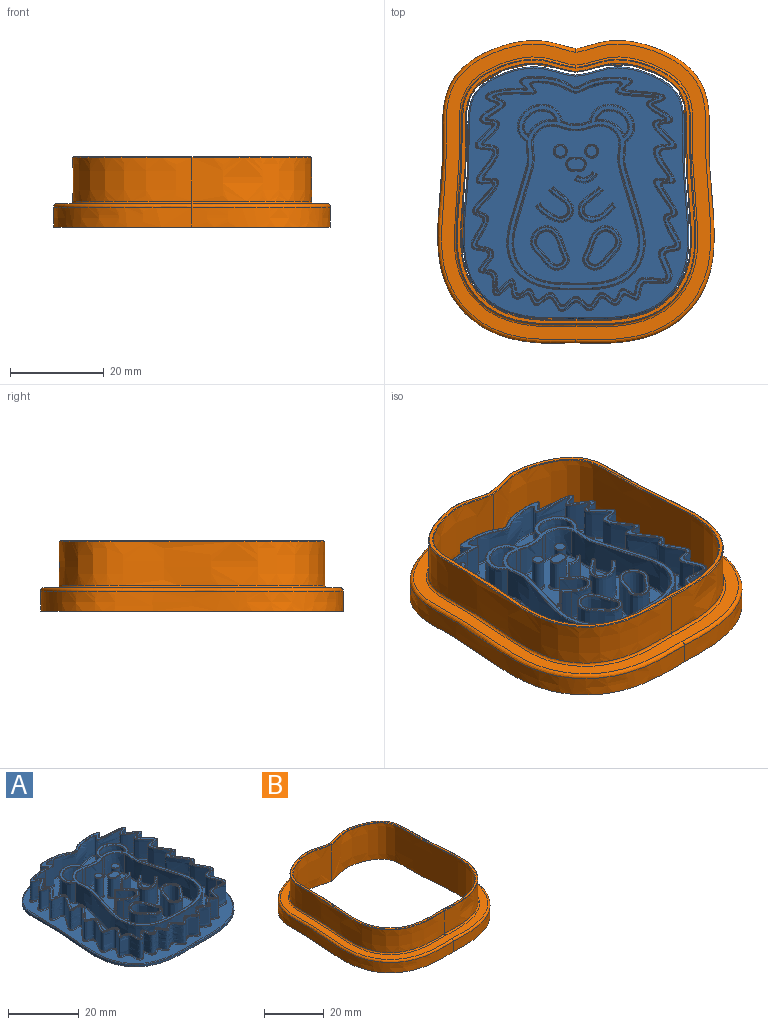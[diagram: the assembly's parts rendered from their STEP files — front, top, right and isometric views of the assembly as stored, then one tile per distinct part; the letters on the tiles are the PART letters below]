
ASSEMBLY  parts=2 mates=1
PART A: 226 faces, bbox 49.6x68.9x8 mm
  f0: plane 7.28x6.69mm, normal (0,0,1), area 7.5mm2, adj f74,f75,f76,f77,f78,f79,f216,f219
  f1: plane 7.12x6.63mm, normal (0,0,1), area 7.4mm2, adj f70,f71,f72,f73,f204,f207,f210,f213
  f2: plane 3.89x1.54mm, normal (0,0,1), area 2mm2, adj f66,f67,f68,f69,f192,f195,f198,f201
  f3: plane 33.51x26.61mm, normal (0,0,1), area 534.3mm2, adj f106,f107,f109,f110,f111,f112,f158,f161
  f4: plane 47.48x42.07mm, normal (0,0,1), area 601.2mm2, adj f127,f129,f130,f131,f132,f133,f135,f136
  f5: extruded ~7.08x6.63mm, area 83.7mm2, adj f18,f95,f175
  f6: extruded ~6.63x5.04mm, area 42.3mm2, adj f7,f15,f87,f181
  f7: extruded ~31.01x27.09mm, area 546.2mm2, adj f6,f8,f89,f179
  f8: extruded ~6.63x5.04mm, area 42.3mm2, adj f7,f9,f88,f177
  f9: extruded ~6.63x0.98mm, area 6.6mm2, adj f8,f10,f86,f176
  f10: extruded ~6.63x6.61mm, area 45mm2, adj f9,f15,f84,f178
  f11: extruded ~31.58x29.07mm, area 560mm2, adj f12,f16,f92,f185
  f12: extruded ~9.09x7.8mm, area 115.3mm2, adj f11,f13,f93,f184
  f13: extruded ~6.63x6.36mm, area 43.3mm2, adj f12,f16,f91,f182
  f14: extruded ~6.63x5.97mm, area 48.9mm2, adj f17,f96,f187
  f15: extruded ~6.63x0.98mm, area 6.6mm2, adj f6,f10,f85,f180
  f16: extruded ~9.11x7.69mm, area 114.8mm2, adj f11,f13,f90,f183
  f17: extruded ~7.1x6.63mm, area 83.4mm2, adj f14,f97,f186
  f18: extruded ~6.63x6.01mm, area 49.7mm2, adj f5,f94,f174
  f19: plane 39.03x28.85mm, normal (0,0,1), area 103mm2, adj f84,f85,f86,f87,f88,f89,f90,f91
  f20: plane 6.53x5.07mm, normal (0,0,1), area 14mm2, adj f174,f175
  f21: plane 6.55x4.98mm, normal (0,0,1), area 14mm2, adj f186,f187
  f22: cylinder r=1.25mm len=6.63mm, axis (0,0,-1), area 52mm2, adj f63,f173
  f23: plane 2.25x2.25mm, normal (0,0,1), area 4mm2, adj f63
  f24: cylinder r=1.25mm len=6.63mm, axis (0,0,-1), area 52mm2, adj f64,f172
  f25: plane 2.25x2.25mm, normal (0,0,1), area 4mm2, adj f64
  f26: extruded ~6.89x6.63mm, area 93.2mm2, adj f31,f77,f171,f218
  f27: plane 6.63x0.32mm, normal (-0.7,0.71,0), area 3mm2, adj f79,f169,f215,f218
  f28: extruded ~6.63x5.61mm, area 78.2mm2, adj f29,f78,f167,f215
  f29: extruded ~6.63x1.33mm, area 12.5mm2, adj f28,f76,f166,f221
  f30: plane 6.63x0.37mm, normal (-0.56,0.83,0), area 3mm2, adj f74,f168,f221,f224
  f31: extruded ~6.63x1.51mm, area 14.1mm2, adj f26,f75,f170,f224
  f32: plane 6.63x0.32mm, normal (0.7,0.71,0), area 3mm2, adj f71,f165,f206,f212
  f33: extruded ~7.31x6.84mm, area 105.4mm2, adj f73,f164,f203,f206
  f34: plane 6.63x0.36mm, normal (0.8,0.6,0), area 3mm2, adj f72,f162,f203,f209
  f35: extruded ~6.63x6.09mm, area 90.5mm2, adj f70,f163,f209,f212
  f36: extruded ~8.98x7.77mm, area 170.1mm2, adj f81,f161
  f37: extruded ~7.48x6.63mm, area 139.1mm2, adj f80,f160
  f38: plane 8.76x7.53mm, normal (0,0,1), area 11.7mm2, adj f80,f81
  f39: plane 7x5.78mm, normal (0,0,1), area 24.2mm2, adj f160
  f40: extruded ~7.49x6.63mm, area 139mm2, adj f83,f159
  f41: extruded ~8.98x7.72mm, area 169.9mm2, adj f82,f158
  f42: plane 8.76x7.53mm, normal (0,0,1), area 11.6mm2, adj f82,f83
  f43: plane 7x5.78mm, normal (0,0,1), area 24.2mm2, adj f159
  f44: extruded ~6.63x3.82mm, area 41.3mm2, adj f45,f50,f103,f157
  f45: extruded ~42.16x36.83mm, area 761.9mm2, adj f44,f46,f104,f132,f134,f136,f138,f140
  f46: extruded ~6.63x5.44mm, area 60.5mm2, adj f45,f47,f102,f127,f128,f130
  f47: extruded ~6.63x3.41mm, area 24.2mm2, adj f46,f48,f100,f129
  f48: extruded ~6.63x1.59mm, area 12.5mm2, adj f47,f49,f98,f131
  f49: extruded ~6.63x2.89mm, area 20mm2, adj f48,f50,f99,f133
  f50: extruded ~39.74x27.91mm, area 510.5mm2, adj f44,f49,f101,f135,f137,f139,f141,f143
  f51: extruded ~48.69x44.19mm, area 1504.8mm2, adj f105,f113,f114,f115,f116,f117,f118,f119
  f52: plane 49.53x44.1mm, normal (0,0,1), area 151.5mm2, adj f98,f99,f100,f101,f102,f103,f104,f105
  f53: plane 54.44x48.98mm, normal (0,0,-1), area 2351.4mm2, adj f54,f55
  f54: extruded ~53.88x24.13mm, area 66.9mm2, adj f53,f55,f188
  f55: extruded ~53.88x24.13mm, area 66.9mm2, adj f53,f54,f189
  f56: plane 53.41x47.81mm, normal (0,0,1), area 531.3mm2, adj f113,f116,f117,f120,f121,f124,f125,f188
  f57: plane 6.63x0.38mm, normal (0.54,0.84,0), area 3mm2, adj f68,f112,f191,f200
  f58: cylinder r=2.36mm len=6.63mm, axis (0,0,-1), area 22.5mm2, adj f69,f111,f191,f194
  f59: plane 6.63x0.38mm, normal (-0.85,0.52,0), area 3mm2, adj f67,f109,f194,f197
  f60: cylinder r=3.11mm len=6.63mm, axis (0,0,-1), area 30mm2, adj f66,f110,f197,f200
  f61: extruded ~6.63x3.88mm, area 72.1mm2, adj f65,f106,f107,f108
  f62: plane 3.64x2.3mm, normal (0,0,1), area 7.2mm2, adj f65
  f63: torus R=1.12mm, axis (0,0,1), area 1.5mm2, adj f22,f23
  f64: torus R=1.12mm, axis (0,0,1), area 1.5mm2, adj f24,f25
  f65: bspline ~3.89x2.55mm, area 2.1mm2, adj f61,f62
  f66: torus R=2.99mm, axis (0,0,1), area 0.9mm2, adj f2,f60,f198,f201
  f67: cylinder r=0.12mm len=0.45mm, axis (0.52,0.85,0), area 0.1mm2, adj f2,f59,f195,f198
  f68: cylinder r=0.12mm len=0.45mm, axis (0.84,-0.54,0), area 0.1mm2, adj f2,f57,f192,f201
  f69: torus R=2.49mm, axis (0,0,1), area 0.7mm2, adj f2,f58,f192,f195
  f70: bspline ~6.43x5.94mm, area 2.7mm2, adj f1,f35,f210,f213
  f71: cylinder r=0.12mm len=0.41mm, axis (0.71,-0.7,0), area 0.1mm2, adj f1,f32,f207,f213
  f72: cylinder r=0.12mm len=0.44mm, axis (0.6,-0.8,0), area 0.1mm2, adj f1,f34,f204,f210
  f73: bspline ~7.43x6.92mm, area 3.1mm2, adj f1,f33,f204,f207
  f74: cylinder r=0.12mm len=0.44mm, axis (0.83,0.56,0), area 0.1mm2, adj f0,f30,f222,f225
  f75: bspline ~2.35x2.23mm, area 0.4mm2, adj f0,f31,f77,f225
  f76: bspline ~2.31x2.28mm, area 0.4mm2, adj f0,f29,f78,f222
  f77: bspline ~9.59x6.97mm, area 2.7mm2, adj f0,f26,f75,f219
  f78: bspline ~8.04x6.03mm, area 2.3mm2, adj f0,f28,f76,f216
  f79: cylinder r=0.12mm len=0.41mm, axis (0.71,0.7,0), area 0.1mm2, adj f0,f27,f216,f219
  f80: bspline ~7.76x6.53mm, area 4.2mm2, adj f37,f38
  f81: bspline ~9.01x7.78mm, area 5mm2, adj f36,f38
  f82: bspline ~9.01x7.78mm, area 5mm2, adj f41,f42
  f83: bspline ~7.76x6.53mm, area 4.2mm2, adj f40,f42
  f84: bspline ~9.15x1.15mm, area 1.3mm2, adj f10,f19,f85,f86
  f85: bspline ~1.23x0.39mm, area 0.2mm2, adj f15,f19,f84,f87
  f86: bspline ~1.23x0.41mm, area 0.2mm2, adj f9,f19,f84,f88
  f87: bspline ~5.91x4.55mm, area 1.3mm2, adj f6,f19,f85,f89
  f88: bspline ~7.01x4.55mm, area 1.3mm2, adj f8,f19,f86,f89
  f89: bspline ~41.76x27.36mm, area 16.2mm2, adj f7,f19,f87,f88
  f90: bspline ~9.12x7.84mm, area 3.4mm2, adj f16,f19,f91,f92
  f91: bspline ~7.77x1.03mm, area 1.3mm2, adj f13,f19,f90,f93
  f92: bspline ~31.91x29.1mm, area 16.6mm2, adj f11,f19,f90,f93
  f93: bspline ~9.1x7.94mm, area 3.4mm2, adj f12,f19,f91,f92
  f94: bspline ~7.77x7.49mm, area 1.5mm2, adj f18,f19,f95
  f95: bspline ~7.36x6.15mm, area 2.5mm2, adj f5,f19,f94
  f96: bspline ~7.59x3.77mm, area 1.5mm2, adj f14,f19,f97
  f97: bspline ~7.38x6.03mm, area 2.5mm2, adj f17,f19,f96
  f98: bspline ~2.16x1.15mm, area 0.4mm2, adj f48,f52,f99,f100
  f99: bspline ~3.49x0.92mm, area 0.6mm2, adj f49,f52,f98,f101
  f100: bspline ~4.77x0.88mm, area 0.7mm2, adj f47,f52,f98,f102
  f101: bspline ~55.15x40.38mm, area 16.2mm2, adj f50,f52,f99,f103
  f102: bspline ~8.45x3.84mm, area 1.8mm2, adj f46,f52,f100,f104
  f103: bspline ~5.97x5.06mm, area 1.2mm2, adj f44,f52,f101,f104
  f104: bspline ~62.83x39.23mm, area 20.6mm2, adj f45,f52,f102,f103
  f105: bspline ~49.78x44.35mm, area 43.4mm2, adj f51,f52
  f106: bspline ~3.05x2.34mm, area 2.3mm2, adj f3,f61,f107,f108
  f107: bspline ~3.06x2.82mm, area 2.2mm2, adj f3,f61,f106,f108
  f108: bspline ~0.25x0.25mm, area 0mm2, adj f61,f106,f107
  f109: cylinder r=0.25mm len=1.2mm, axis (0.52,0.85,0), area 0.3mm2, adj f3,f59,f193,f196
  f110: torus R=3.36mm, axis (0,0,1), area 2mm2, adj f3,f60,f196,f199
  f111: torus R=2.11mm, axis (0,0,1), area 1.4mm2, adj f3,f58,f190,f193
  f112: cylinder r=0.25mm len=1.19mm, axis (0.84,-0.54,0), area 0.3mm2, adj f3,f57,f190,f199
  f113: bspline ~8.76x3.44mm, area 4.7mm2, adj f51,f56,f114,f115
  f114: bspline ~0.39x0.25mm, area 0.1mm2, adj f51,f113,f116
  f115: bspline ~0.3x0.26mm, area 0.1mm2, adj f51,f113,f117
  f116: bspline ~24.09x2.84mm, area 11.6mm2, adj f51,f56,f114,f118
  f117: bspline ~4.56x4.06mm, area 3.2mm2, adj f51,f56,f115,f119
  f118: bspline ~0.32x0.28mm, area 0.1mm2, adj f51,f116,f120
  f119: bspline ~0.27x0.26mm, area 0.1mm2, adj f51,f117,f121
  f120: bspline ~9.09x3.38mm, area 4.8mm2, adj f51,f56,f118,f122
  f121: bspline ~12.78x4.1mm, area 8.4mm2, adj f51,f56,f119,f123
  f122: bspline ~0.31x0.27mm, area 0.1mm2, adj f51,f120,f124
  f123: bspline ~0.25x0.25mm, area 0mm2, adj f51,f121,f125
  f124: bspline ~44.36x36.48mm, area 39.1mm2, adj f51,f56,f122,f126
  f125: bspline ~24.17x8.49mm, area 14.3mm2, adj f51,f56,f123,f126
  f126: bspline ~0.3x0.27mm, area 0.1mm2, adj f51,f124,f125
  f127: bspline ~7.1x0.96mm, area 2.1mm2, adj f4,f46,f128,f129
  f128: bspline ~0.34x0.33mm, area 0.1mm2, adj f46,f127,f130
  f129: bspline ~5.39x1.22mm, area 1.5mm2, adj f4,f47,f127,f131
  f130: bspline ~2.99x2.52mm, area 1.3mm2, adj f4,f46,f128,f132
  f131: bspline ~1.77x1.2mm, area 0.7mm2, adj f4,f48,f129,f133
  f132: bspline ~4.66x3.67mm, area 1.7mm2, adj f4,f45,f130,f134
  f133: bspline ~4.3x0.55mm, area 1.1mm2, adj f4,f49,f131,f135
  f134: bspline ~0.33x0.29mm, area 0.1mm2, adj f45,f132,f136
  f135: bspline ~21.05x2.87mm, area 6.8mm2, adj f4,f50,f133,f137
  f136: bspline ~5.48x3.69mm, area 3.3mm2, adj f4,f45,f134,f138
  f137: bspline ~0.28x0.25mm, area 0mm2, adj f50,f135,f139
  f138: bspline ~0.3x0.27mm, area 0.1mm2, adj f45,f136,f140
  f139: bspline ~9.08x3.15mm, area 4.2mm2, adj f4,f50,f137,f141
  f140: bspline ~7.57x3.45mm, area 4.2mm2, adj f4,f45,f138,f142
  f141: bspline ~0.65x0.25mm, area 0.1mm2, adj f50,f139,f143
  f142: bspline ~0.25x0.25mm, area 0mm2, adj f45,f140,f144
  f143: bspline ~4.92x4.23mm, area 3mm2, adj f4,f50,f141,f145
  f144: bspline ~19.49x4.75mm, area 11mm2, adj f4,f45,f142,f146
  f145: bspline ~0.35x0.29mm, area 0.1mm2, adj f50,f143,f147
  f146: bspline ~0.28x0.26mm, area 0.1mm2, adj f45,f144,f148
  f147: bspline ~5.47x3.68mm, area 3.3mm2, adj f4,f50,f145,f149
  f148: bspline ~4.77x2.89mm, area 2.4mm2, adj f4,f45,f146,f150
  f149: bspline ~0.3x0.27mm, area 0.1mm2, adj f50,f147,f151
  f150: bspline ~0.3x0.27mm, area 0.1mm2, adj f45,f148,f152
  f151: bspline ~7.58x3.48mm, area 4.2mm2, adj f4,f50,f149,f153
  f152: bspline ~29.44x5.83mm, area 15.8mm2, adj f4,f45,f150,f154
  f153: bspline ~0.25x0.25mm, area 0mm2, adj f50,f151,f155
  f154: bspline ~0.25x0.25mm, area 0mm2, adj f45,f152,f156
  f155: bspline ~19.83x4.72mm, area 10.6mm2, adj f4,f50,f153,f157
  f156: bspline ~5.14x3.79mm, area 2.2mm2, adj f4,f45,f154,f157
  f157: bspline ~5.75x4.73mm, area 2.4mm2, adj f4,f44,f155,f156
  f158: bspline ~9.51x8.28mm, area 10.3mm2, adj f3,f41
  f159: bspline ~7.5x6.28mm, area 8mm2, adj f40,f43
  f160: bspline ~7.51x6.28mm, area 8mm2, adj f37,f39
  f161: bspline ~9.51x8.28mm, area 10.3mm2, adj f3,f36
  f162: cylinder r=0.25mm len=1.15mm, axis (0.6,-0.8,0), area 0.3mm2, adj f3,f34,f202,f208
  f163: bspline ~6.51x6.01mm, area 5.4mm2, adj f3,f35,f208,f211
  f164: bspline ~8.6x8.15mm, area 6.5mm2, adj f3,f33,f202,f205
  f165: cylinder r=0.25mm len=1.07mm, axis (0.71,-0.7,0), area 0.3mm2, adj f3,f32,f205,f211
  f166: bspline ~2.8x2.66mm, area 0.8mm2, adj f3,f29,f167,f220
  f167: bspline ~6.07x5.54mm, area 4.6mm2, adj f3,f28,f166,f214
  f168: cylinder r=0.25mm len=1.18mm, axis (0.83,0.56,0), area 0.3mm2, adj f3,f30,f220,f223
  f169: cylinder r=0.25mm len=1.07mm, axis (0.71,0.7,0), area 0.3mm2, adj f3,f27,f214,f217
  f170: bspline ~3.17x3.01mm, area 0.9mm2, adj f3,f31,f171,f223
  f171: bspline ~9.86x7.82mm, area 5.7mm2, adj f3,f26,f170,f217
  f172: torus R=1.5mm, axis (0,0,1), area 3.3mm2, adj f3,f24
  f173: torus R=1.5mm, axis (0,0,1), area 3.3mm2, adj f3,f22
  f174: bspline ~6.77x3.98mm, area 2.9mm2, adj f18,f20,f175
  f175: bspline ~7.13x6.12mm, area 4.7mm2, adj f5,f20,f174
  f176: bspline ~1.23x0.52mm, area 0.4mm2, adj f3,f9,f177,f178
  f177: bspline ~6.55x3.41mm, area 2.5mm2, adj f3,f8,f176,f179
  f178: bspline ~9.88x1.63mm, area 2.7mm2, adj f3,f10,f176,f180
  f179: bspline ~41.45x27.11mm, area 32.3mm2, adj f3,f7,f177,f181
  f180: bspline ~1.24x0.51mm, area 0.4mm2, adj f3,f15,f178,f181
  f181: bspline ~6.81x4.45mm, area 2.5mm2, adj f3,f6,f179,f180
  f182: bspline ~6.75x0.96mm, area 2.5mm2, adj f4,f13,f183,f184
  f183: bspline ~9.62x8.18mm, area 6.9mm2, adj f4,f16,f182,f185
  f184: bspline ~9.6x8.37mm, area 6.9mm2, adj f4,f12,f182,f185
  f185: bspline ~32.05x29.63mm, area 33.3mm2, adj f4,f11,f183,f184
  f186: bspline ~7.2x6.05mm, area 4.7mm2, adj f17,f21,f187
  f187: bspline ~7.48x3.8mm, area 2.8mm2, adj f14,f21,f186
  f188: bspline ~53.91x25.31mm, area 34.9mm2, adj f54,f56,f189
  f189: bspline ~53.91x25.31mm, area 34.9mm2, adj f55,f56,f188
  f190: bspline ~0.47x0.28mm, area 0mm2, adj f111,f112,f191
  f191: cylinder r=0.15mm len=6.63mm, axis (0,0,-1), area 1.5mm2, adj f57,f58,f190,f192
  f192: torus R=0.03mm, axis (0,0,1), area 0mm2, adj f2,f68,f69,f191
  f193: bspline ~0.48x0.28mm, area 0mm2, adj f109,f111,f194
  f194: cylinder r=0.15mm len=6.63mm, axis (0,0,-1), area 1.5mm2, adj f58,f59,f193,f195
  f195: torus R=0.03mm, axis (0,0,1), area 0mm2, adj f2,f67,f69,f194
  f196: bspline ~0.48x0.27mm, area 0mm2, adj f109,f110,f197
  f197: cylinder r=0.15mm len=6.63mm, axis (0,0,-1), area 1.6mm2, adj f59,f60,f196,f198
  f198: torus R=0.03mm, axis (0,0,1), area 0mm2, adj f2,f66,f67,f197
  f199: bspline ~0.47x0.27mm, area 0mm2, adj f110,f112,f200
  f200: cylinder r=0.15mm len=6.63mm, axis (0,0,-1), area 1.6mm2, adj f57,f60,f199,f201
  f201: torus R=0.03mm, axis (0,0,1), area 0mm2, adj f2,f66,f68,f200
  f202: bspline ~0.45x0.28mm, area 0mm2, adj f162,f164,f203
  f203: cylinder r=0.15mm len=6.63mm, axis (0,0,-1), area 1.4mm2, adj f33,f34,f202,f204
  f204: torus R=0.03mm, axis (0,0,1), area 0mm2, adj f1,f72,f73,f203
  f205: bspline ~0.46x0.27mm, area 0mm2, adj f164,f165,f206
  f206: cylinder r=0.15mm len=6.63mm, axis (0,0,-1), area 1.5mm2, adj f32,f33,f205,f207
  f207: torus R=0.03mm, axis (0,0,1), area 0mm2, adj f1,f71,f73,f206
  f208: bspline ~0.48x0.29mm, area 0mm2, adj f162,f163,f209
  f209: cylinder r=0.15mm len=6.63mm, axis (0,0,-1), area 1.7mm2, adj f34,f35,f208,f210
  f210: torus R=0.03mm, axis (0,0,1), area 0mm2, adj f1,f70,f72,f209
  f211: bspline ~0.46x0.27mm, area 0mm2, adj f163,f165,f212
  f212: cylinder r=0.15mm len=6.63mm, axis (0,0,-1), area 1.6mm2, adj f32,f35,f211,f213
  f213: torus R=0.03mm, axis (0,0,1), area 0mm2, adj f1,f70,f71,f212
  f214: bspline ~0.46x0.27mm, area 0mm2, adj f167,f169,f215
  f215: cylinder r=0.15mm len=6.63mm, axis (0,0,-1), area 1.6mm2, adj f27,f28,f214,f216
  f216: torus R=0.03mm, axis (0,0,1), area 0mm2, adj f0,f78,f79,f215
  f217: bspline ~0.46x0.27mm, area 0mm2, adj f169,f171,f218
  f218: cylinder r=0.15mm len=6.63mm, axis (0,0,-1), area 1.5mm2, adj f26,f27,f217,f219
  f219: torus R=0.03mm, axis (0,0,1), area 0mm2, adj f0,f77,f79,f218
  f220: bspline ~0.48x0.27mm, area 0mm2, adj f166,f168,f221
  f221: cylinder r=0.15mm len=6.63mm, axis (0,0,-1), area 1.6mm2, adj f29,f30,f220,f222
  f222: torus R=0.03mm, axis (0,0,1), area 0mm2, adj f0,f74,f76,f221
  f223: bspline ~0.47x0.27mm, area 0mm2, adj f168,f170,f224
  f224: cylinder r=0.15mm len=6.63mm, axis (0,0,-1), area 1.5mm2, adj f30,f31,f223,f225
  f225: torus R=0.03mm, axis (0,0,1), area 0mm2, adj f0,f74,f75,f224
PART B: 17 faces, bbox 59.1x64.7x15 mm
  f0: extruded ~56.68x25.53mm, area 875.4mm2, adj f3,f10,f16
  f1: extruded ~54.68x24.53mm, area 1344mm2, adj f2,f5,f11
  f2: extruded ~54.68x24.53mm, area 1344mm2, adj f1,f5,f12
  f3: extruded ~56.68x25.53mm, area 875.4mm2, adj f0,f9,f15
  f4: plane 56.45x50.84mm, normal (0,0,1), area 155.7mm2, adj f9,f10,f11,f12
  f5: plane 64.7x59.1mm, normal (0,0,-1), area 983.1mm2, adj f1,f2,f6,f7
  f6: extruded ~64.69x29.53mm, area 450.8mm2, adj f5,f7,f14
  f7: extruded ~64.69x29.53mm, area 450.8mm2, adj f5,f6,f13
  f8: plane 63.21x57.61mm, normal (0,0,1), area 547.2mm2, adj f13,f14,f15,f16
  f9: bspline ~56.75x28.12mm, area 19.6mm2, adj f3,f4,f10
  f10: bspline ~56.75x28.12mm, area 19.6mm2, adj f0,f4,f9
  f11: bspline ~55.08x27.25mm, area 19.3mm2, adj f1,f4,f12
  f12: bspline ~55.08x27.16mm, area 19.3mm2, adj f2,f4,f11
  f13: bspline ~64.71x29.93mm, area 124.1mm2, adj f7,f8,f14
  f14: bspline ~64.71x29.93mm, area 124.1mm2, adj f6,f8,f13
  f15: bspline ~57.7x28.4mm, area 74mm2, adj f3,f8,f16
  f16: bspline ~57.71x28.01mm, area 74mm2, adj f0,f8,f15
PLACE A t=(-60.17,-62.43,-6.1)mm
PLACE B t=(-60.17,-67.16,-10.1)mm
MATE fastened A.f53 <-> B.f5  axis (0,0,-1) through (-60.17,-29.47,-5.1)mm
